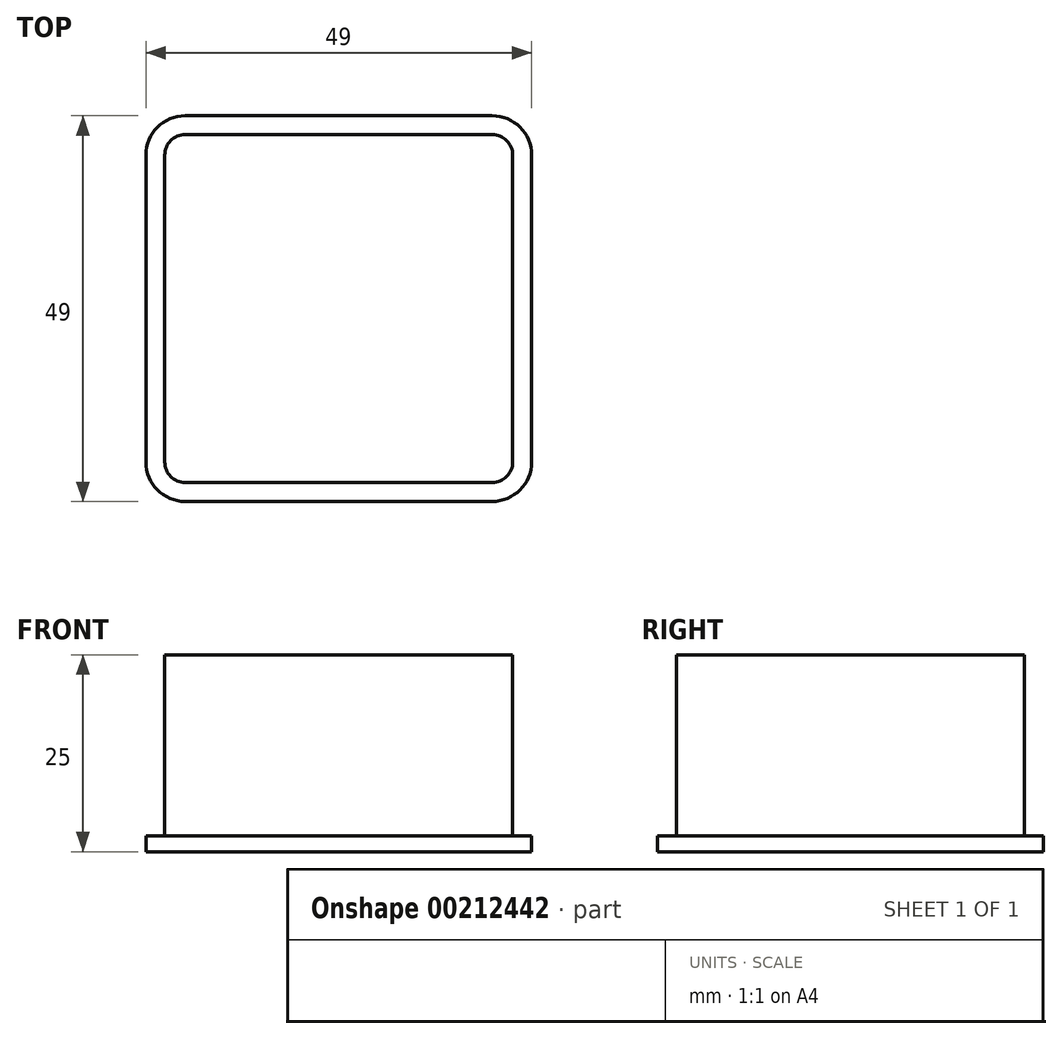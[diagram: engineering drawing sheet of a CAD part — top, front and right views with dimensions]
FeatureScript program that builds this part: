
annotation { "Feature Type Name" : "Feature", "Feature Type Description" : "" }
export const myFeature = defineFeature(function(context is Context, id is Id, definition is map)
    precondition{}
    {
        {
            var Q0;
            Q0=qCreatedBy(makeId("Top.planeOp"),FACE);
            var sketch = newSketch(context, id + "F0", { "sketchPlane" : qUnion([Q0])});
            skLineSegment(sketch, "E0.bottom", {"start": v(19.5, 19.5) * mm, "end": v(-19.5, 19.5) * mm, "construction": true});
            skLineSegment(sketch, "E0.top", {"start": v(19.5, -19.5) * mm, "end": v(-19.5, -19.5) * mm, "construction": true});
            skLineSegment(sketch, "E0.left", {"start": v(19.5, 19.5) * mm, "end": v(19.5, -19.5) * mm, "construction": true});
            skLineSegment(sketch, "E0.right", {"start": v(-19.5, 19.5) * mm, "end": v(-19.5, -19.5) * mm, "construction": true});
            skPoint(sketch, "E0.middle", {"position": v(0, 0) * mm});
            skArc(sketch, "E1", {"start": v(-22.1, 19.5) * mm, "mid": v(-21.34, 21.34) * mm, "end": v(-19.5, 22.1) * mm});
            skArc(sketch, "E2", {"start": v(-24.5, 19.5) * mm, "mid": v(-23.04, 23.04) * mm, "end": v(-19.5, 24.5) * mm});
            skArc(sketch, "E3.MirrorCS", {"start": v(22.1, 19.5) * mm, "mid": v(21.34, 21.34) * mm, "end": v(19.5, 22.1) * mm});
            skArc(sketch, "E4.MirrorCS", {"start": v(24.5, 19.5) * mm, "mid": v(23.04, 23.04) * mm, "end": v(19.5, 24.5) * mm});
            skLineSegment(sketch, "E5", {"start": v(-19.5, 24.5) * mm, "end": v(19.5, 24.5) * mm});
            skLineSegment(sketch, "E6", {"start": v(19.5, 22.1) * mm, "end": v(-19.5, 22.1) * mm});
            skArc(sketch, "E7.MirrorCS", {"start": v(-24.5, -19.5) * mm, "mid": v(-23.04, -23.04) * mm, "end": v(-19.5, -24.5) * mm});
            skArc(sketch, "E8.MirrorCS", {"start": v(-22.1, -19.5) * mm, "mid": v(-21.34, -21.34) * mm, "end": v(-19.5, -22.1) * mm});
            skLineSegment(sketch, "E9.MirrorCS", {"start": v(19.5, -22.1) * mm, "end": v(-19.5, -22.1) * mm});
            skLineSegment(sketch, "E10.MirrorCS", {"start": v(-19.5, -24.5) * mm, "end": v(19.5, -24.5) * mm});
            skArc(sketch, "E11.MirrorCS", {"start": v(24.5, -19.5) * mm, "mid": v(23.04, -23.04) * mm, "end": v(19.5, -24.5) * mm});
            skArc(sketch, "E12.MirrorCS", {"start": v(22.1, -19.5) * mm, "mid": v(21.34, -21.34) * mm, "end": v(19.5, -22.1) * mm});
            skLineSegment(sketch, "E13", {"start": v(-24.5, 19.5) * mm, "end": v(-24.5, -19.5) * mm});
            skLineSegment(sketch, "E14", {"start": v(-22.1, -19.5) * mm, "end": v(-22.1, 19.5) * mm});
            skLineSegment(sketch, "E15", {"start": v(22.1, 19.5) * mm, "end": v(22.1, -19.5) * mm});
            skLineSegment(sketch, "E16", {"start": v(24.5, -19.5) * mm, "end": v(24.5, 19.5) * mm});
            skSolve(sketch);
        }
        {
            var Q0;
            Q0=makeQuery(id+"F0.imprint","IMPRINT",FACE,{"disambiguationData":[TD([[makeQuery(id+"F0.imprint","IMPRINT",EDGE,{"derivedFrom":sQuery(id+"F0.wireOp",EDGE,"E1")}),1.0]])]});
            extrude(context, id + "F1", {"entities" : qUnion([Q0]), "depth" : 25 * mm, "offsetDistance" : 25 * mm});
        }
        {
            var Q0;
            Q0=makeQuery(id+"F0.imprint","IMPRINT",FACE,{"disambiguationData":[TD([[makeQuery(id+"F0.imprint","IMPRINT",EDGE,{"derivedFrom":sQuery(id+"F0.wireOp",EDGE,"E1")}),-1.0]])]});
            extrude(context, id + "F2", {"entities" : qUnion([Q0]), "operationType" : NewBodyOperationType.ADD, "depth" : 2 * mm, "offsetDistance" : 25 * mm});
        }
    });
